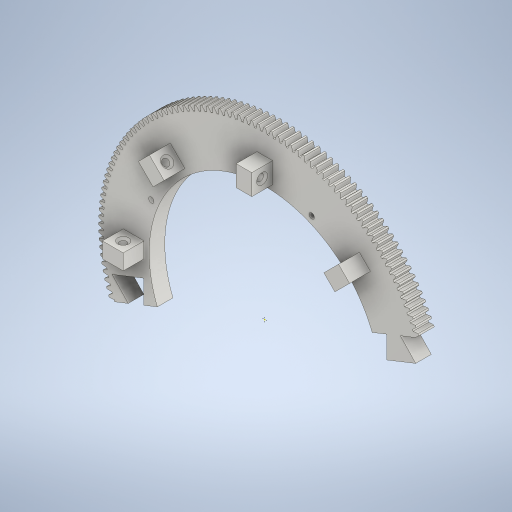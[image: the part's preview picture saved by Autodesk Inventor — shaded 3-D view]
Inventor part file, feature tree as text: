
AUTODESK INVENTOR PART (.ipt)
format: ipt  version: 2023 (Build 270158000, 158)  size: 2,501,632 bytes
history: native  units: mm (DEFAULTED — no unit token found)
features: sketch x7, extrude x5, plane x3, other x3, pattern_circular x2, chamfer x1, hole x1, projected_geometry x1
ambient origin geometry x8: Origin, YZ Plane, XZ Plane, XY Plane, X Axis, Y Axis, Z Axis, Center Point
bodies: Solid1 (feature_tree)
feature tree (23):
  extrude  "Extrusion1"  Depth=15.0mm TaperAngle=0.0deg
  plane  "Work Plane2"
  plane  "Work Plane8"
  plane  "Work Plane9"
  other  "Spur Gear"
  extrude  "Extrusion2"  Depth=10.0mm TaperAngle=0.0deg
  extrude  "Extrusion4"  Depth=0.19635mm TaperAngle=0.0deg
  extrude  "Extrusion5"  TaperAngle=0.0deg  [1 undecoded]
  chamfer  "Chamfer1"  [1 undecoded]
  pattern_circular  "Circular Pattern3"  Count=25  [1 undecoded]
  hole  "Hole2"  [1 undecoded]
  pattern_circular  "Circular Pattern4"  [2 undecoded]
  extrude  "Extrusion7"  Depth=20.0mm
  sketch  "Sketch12"  dims[d50=222.5mm d51=15.0mm d52=0.0mm d75=7.5mm d76=20.0mm d77=15.0mm d78=20.0mm d79=20.0mm d80=0.0mm d81=6.5mm d82=20.0mm d83=0.0mm d87=2.0mm d88=2.0mm d89=45.0deg d90=80.0mm d91=360.0deg d110=5.0mm d111=67.5deg d112=5.0mm d113=6.0mm d114=4.0mm d115=2.0mm d116=90.0deg d117=8.0mm d118=20.594885mm d119=40.0mm d120=360.0deg d123=22.125mm d124=20.0mm d125=15.0mm d126=1.0mm d127=1.0mm d128=4.0mm d129=50.0mm d130=0.0mm d106=0.5mm d107=0.872665mm d108=0.5mm d109=0.872665mm]
  sketch  "Sketch1"  dims[d0=320.0mm d1=15.0mm d2=0.0mm]
  sketch  "Sketch2"  dims[d3=320.0mm d4=10.0mm d5=0.0mm]
  other  "Srf1"
  sketch  "Sketch3"  dims[d16=200.0mm d17=0.0mm d34=0.19635mm]
  sketch  "Sketch7"  dims[d39=0.0mm d41=0.0mm]
  sketch  "Sketch8"  dims[d43=200.0mm]
  sketch  "Sketch11"  dims[d46=200.0mm d47=0.0mm d48=0.0mm d49=250.0mm]
  projected_geometry  "Projected Loop3"
  other  "Pitch Diameter"
note: 6 required parameter values undecoded (feature->parameter linkage not recoverable at this tier; creation-order binding heuristic only, values carry confidence <= 0.55)
